# Revit family: Ribbeelement-TT
name_source: partatom
category: Structural Framing
units: mm (PartAtom-declared; Revit-internal decimal feet)

## family parameters
Always export as geometry = No
Always vertical = Yes
Cut with Voids When Loaded = No
Material for Model Behavior = Other
OmniClass Number = 23.25.30.11.14.14
OmniClass Title = Beams
Section Shape = Not Defined
Shared = No
Show family pre-cut in plan views = Yes

## types (11) — shared parameters
CRH_RFA_Bruger_LastRelease = kvnUVH7F
CRH_RFA_Bruger_LastSave = kvnUVH7F
CRH_RFA_TimeStamp_LastRelease = 20230927
CRH_RFA_TimeStamp_LastSave = 20230927
Manufacturer = CRH Concrete
Plade Bredde 1 = 1196 mm  [stored 3.92388 ft]
Plade Bredde 2 = 1196 mm  [stored 3.92388 ft]
Plade Tykkelse = 60 mm  [stored 0.19685 ft]

## per-type parameters (varying)
| type | Højde | Model | Ribbe Bredde | Ribbe CC Afstand |
| TTD 102 | 1020 mm  [stored 3.34646 ft] | TTD | 190 mm | 1276 mm  [stored 4.18635 ft] |
| TT 30 | 300 mm | TT | 180 mm  [stored 0.590551 ft] | 1194 mm |
| TT 40 | 400 mm  [stored 1.31234 ft] | TT | 170 mm  [stored 0.557743 ft] | 1194 mm |
| TT 50 | 500 mm  [stored 1.64042 ft] | TT | 160 mm  [stored 0.524934 ft] | 1194 mm |
| TT 60 | 600 mm | TT | 150 mm | 1194 mm |
| TT 76 | 760 mm | TT | 150 mm | 1210 mm  [stored 3.96982 ft] |
| TTD 40 | 400 mm  [stored 1.31234 ft] | TTD | 190 mm | 1214 mm  [stored 3.98294 ft] |
| TTD 50 | 500 mm  [stored 1.64042 ft] | TTD | 190 mm | 1224 mm  [stored 4.01575 ft] |
| TTD 60 | 600 mm | TTD | 190 mm | 1234 mm  [stored 4.04856 ft] |
| TTD 76 | 760 mm | TTD | 190 mm | 1250 mm  [stored 4.10105 ft] |
| TTD 90 | 900 mm  [stored 2.95276 ft] | TTD | 190 mm | 1264 mm |

note: [stored X ft] marks values corroborated as IEEE doubles in the binary element streams (Revit-internal decimal feet)

## geometry (parser evidence)
native form markers: Sweep x3
no freeform markers — native parametric forms only
